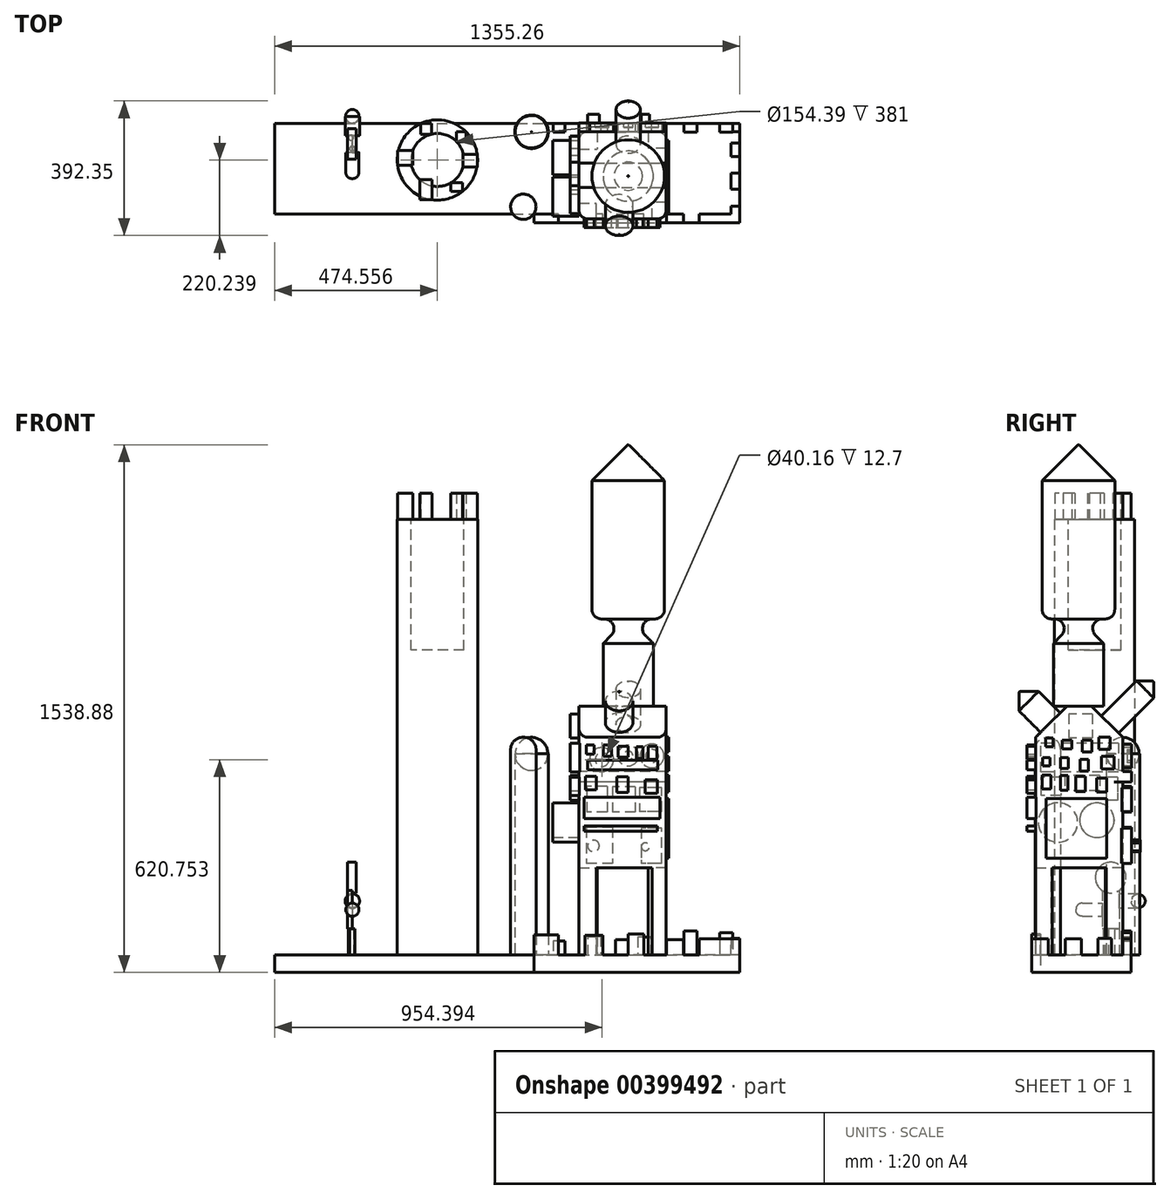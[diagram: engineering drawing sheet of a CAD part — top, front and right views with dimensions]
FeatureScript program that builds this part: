
annotation { "Feature Type Name" : "Feature", "Feature Type Description" : "" }
export const myFeature = defineFeature(function(context is Context, id is Id, definition is map)
    precondition{}
    {
        {
            var Q0;
            Q0=qCreatedBy(makeId("Front.planeOp"),FACE);
            var sketch = newSketch(context, id + "F0", { "sketchPlane" : qUnion([Q0])});
            skLineSegment(sketch, "E0.bottom", {"start": v(-143.4, 414.63) * mm, "end": v(110.6, 414.63) * mm});
            skLineSegment(sketch, "E0.top", {"start": v(-143.4, -93.37) * mm, "end": v(110.6, -93.37) * mm});
            skLineSegment(sketch, "E0.left", {"start": v(-143.4, 414.63) * mm, "end": v(-143.4, -93.37) * mm});
            skLineSegment(sketch, "E0.right", {"start": v(110.6, 414.63) * mm, "end": v(110.6, -93.37) * mm});
            skSolve(sketch);
        }
        {
            var Q0;
            Q0 = qSketchRegion(id + "F0", true);
            extrude(context, id + "F1", {"entities" : qUnion([Q0]), "depth" : 254 * mm});
        }
        {
            var Q0;
            Q0=makeQuery(id+"F1.opExtrude","CAP_EDGE",EDGE,{"disambiguationData":[OSD([sQuery(id+"F0.wireOp",EDGE,"E0.bottom")])],"isStart":false});
            chamfer(context, id + "F2", {"entities" : qUnion([Q0]), "width" : 127 * mm, "tangentPropagation" : true});
        }
        {
            var Q0;
            Q0=makeQuery(id+"F1.opExtrude","CAP_EDGE",EDGE,{"disambiguationData":[OSD([sQuery(id+"F0.wireOp",EDGE,"E0.bottom")])],"isStart":true});
            chamfer(context, id + "F3", {"entities" : qUnion([Q0]), "width" : 127 * mm, "tangentPropagation" : true});
        }
        {
            var Q0;
            {var subQ0=sQuery(id+"F0.wireOp",EDGE,"E0.bottom");Q0=makeQuery(id+"F3.opChamfer","BLEND_EDGE",EDGE,{"blendedFrom":[makeQuery(id+"F1.opExtrude","CAP_EDGE",EDGE,{"disambiguationData":[OSD([subQ0])],"isStart":true}),makeQuery(id+"F2.opChamfer","BLEND_FACE",FACE,{"disambiguationData":[OSD([subQ0])]})],"blendedInto":[makeQuery(id+"F2.opChamfer","BLEND_FACE",FACE,{"disambiguationData":[OSD([subQ0])]})]});}
            chamfer(context, id + "F4", {"entities" : qUnion([Q0]), "width" : 50.8 * mm, "tangentPropagation" : true});
        }
        {
            var Q0;
            Q0=makeQuery(id+"F4.opChamfer","BLEND_FACE",FACE,{"disambiguationData":[OSD([sQuery(id+"F0.wireOp",EDGE,"E0.bottom")])]});
            var sketch = newSketch(context, id + "F5", { "sketchPlane" : qUnion([Q0])});
            skCircle(sketch, "E1", {"center": v(0, -129.26) * mm, "radius": 73.19 * mm});
            skSolve(sketch);
        }
        {
            var Q0;
            Q0 = qSketchRegion(id + "F5", true);
            extrude(context, id + "F6", {"entities" : qUnion([Q0]), "operationType" : NewBodyOperationType.ADD, "depth" : 254 * mm});
        }
        {
            var Q0;
            Q0=makeQuery(id+"F6.opExtrude","CAP_EDGE",EDGE,{"disambiguationData":[OSD([sQuery(id+"F5.wireOp",EDGE,"E1")])],"isStart":false});
            chamfer(context, id + "F7", {"entities" : qUnion([Q0]), "width" : 71.12 * mm, "tangentPropagation" : true});
        }
        {
            var Q0;
            Q0=makeQuery(id+"F1.opExtrude","SWEPT_FACE",FACE,{"disambiguationData":[OSD([sQuery(id+"F0.wireOp",EDGE,"E0.right")])]});
            var sketch = newSketch(context, id + "F8", { "sketchPlane" : qUnion([Q0])});
            skLineSegment(sketch, "E2.bottom", {"start": v(-225.22, 286.05) * mm, "end": v(-203.04, 286.05) * mm});
            skLineSegment(sketch, "E2.top", {"start": v(-225.22, 259.97) * mm, "end": v(-203.04, 259.97) * mm});
            skLineSegment(sketch, "E2.left", {"start": v(-225.22, 286.05) * mm, "end": v(-225.22, 259.97) * mm});
            skLineSegment(sketch, "E2.right", {"start": v(-203.04, 286.05) * mm, "end": v(-203.04, 259.97) * mm});
            skLineSegment(sketch, "E3.bottom", {"start": v(-176.84, 279.59) * mm, "end": v(-149.3, 279.59) * mm});
            skLineSegment(sketch, "E3.top", {"start": v(-176.84, 254.16) * mm, "end": v(-149.3, 254.16) * mm});
            skLineSegment(sketch, "E3.left", {"start": v(-176.84, 279.59) * mm, "end": v(-176.84, 254.16) * mm});
            skLineSegment(sketch, "E3.right", {"start": v(-149.3, 279.59) * mm, "end": v(-149.3, 254.16) * mm});
            skLineSegment(sketch, "E4.bottom", {"start": v(-118.38, 279.83) * mm, "end": v(-89.7, 279.83) * mm});
            skLineSegment(sketch, "E4.top", {"start": v(-118.38, 244.95) * mm, "end": v(-89.7, 244.95) * mm});
            skLineSegment(sketch, "E4.left", {"start": v(-118.38, 279.83) * mm, "end": v(-118.38, 244.95) * mm});
            skLineSegment(sketch, "E4.right", {"start": v(-89.7, 279.83) * mm, "end": v(-89.7, 244.95) * mm});
            skLineSegment(sketch, "E5.bottom", {"start": v(-70.45, 288.39) * mm, "end": v(-36.24, 288.39) * mm});
            skLineSegment(sketch, "E5.top", {"start": v(-70.45, 252.8) * mm, "end": v(-36.24, 252.8) * mm});
            skLineSegment(sketch, "E5.left", {"start": v(-70.45, 288.39) * mm, "end": v(-70.45, 252.8) * mm});
            skLineSegment(sketch, "E5.right", {"start": v(-36.24, 288.39) * mm, "end": v(-36.24, 252.8) * mm});
            skLineSegment(sketch, "E6.bottom", {"start": v(-233.3, 228.9) * mm, "end": v(-212.62, 228.9) * mm});
            skLineSegment(sketch, "E6.top", {"start": v(-233.3, 204) * mm, "end": v(-212.62, 204) * mm});
            skLineSegment(sketch, "E6.left", {"start": v(-233.3, 228.9) * mm, "end": v(-233.3, 204) * mm});
            skLineSegment(sketch, "E6.right", {"start": v(-212.62, 228.9) * mm, "end": v(-212.62, 204) * mm});
            skLineSegment(sketch, "E7.bottom", {"start": v(-181.54, 228.33) * mm, "end": v(-158.71, 228.33) * mm});
            skLineSegment(sketch, "E7.top", {"start": v(-181.54, 196.85) * mm, "end": v(-158.71, 196.85) * mm});
            skLineSegment(sketch, "E7.left", {"start": v(-181.54, 228.33) * mm, "end": v(-181.54, 196.85) * mm});
            skLineSegment(sketch, "E7.right", {"start": v(-158.71, 228.33) * mm, "end": v(-158.71, 196.85) * mm});
            skLineSegment(sketch, "E8.bottom", {"start": v(-125.12, 222.84) * mm, "end": v(-100.62, 222.84) * mm});
            skLineSegment(sketch, "E8.top", {"start": v(-125.12, 188.82) * mm, "end": v(-100.62, 188.82) * mm});
            skLineSegment(sketch, "E8.left", {"start": v(-125.12, 222.84) * mm, "end": v(-125.12, 188.82) * mm});
            skLineSegment(sketch, "E8.right", {"start": v(-100.62, 222.84) * mm, "end": v(-100.62, 188.82) * mm});
            skLineSegment(sketch, "E9.bottom", {"start": v(-62.28, 231.84) * mm, "end": v(-25.23, 231.84) * mm});
            skLineSegment(sketch, "E9.top", {"start": v(-62.28, 195.23) * mm, "end": v(-25.23, 195.23) * mm});
            skLineSegment(sketch, "E9.left", {"start": v(-62.28, 231.84) * mm, "end": v(-62.28, 195.23) * mm});
            skLineSegment(sketch, "E9.right", {"start": v(-25.23, 231.84) * mm, "end": v(-25.23, 195.23) * mm});
            skLineSegment(sketch, "E10.bottom", {"start": v(-235.32, 177.96) * mm, "end": v(-210, 177.96) * mm});
            skLineSegment(sketch, "E10.top", {"start": v(-235.32, 137.2) * mm, "end": v(-210, 137.2) * mm});
            skLineSegment(sketch, "E10.left", {"start": v(-235.32, 177.96) * mm, "end": v(-235.32, 137.2) * mm});
            skLineSegment(sketch, "E10.right", {"start": v(-210, 177.96) * mm, "end": v(-210, 137.2) * mm});
            skLineSegment(sketch, "E11.bottom", {"start": v(-181.54, 175.72) * mm, "end": v(-160.61, 175.72) * mm});
            skLineSegment(sketch, "E11.top", {"start": v(-181.54, 133.6) * mm, "end": v(-160.61, 133.6) * mm});
            skLineSegment(sketch, "E11.left", {"start": v(-181.54, 175.72) * mm, "end": v(-181.54, 133.6) * mm});
            skLineSegment(sketch, "E11.right", {"start": v(-160.61, 175.72) * mm, "end": v(-160.61, 133.6) * mm});
            skLineSegment(sketch, "E12.bottom", {"start": v(-136.85, 173.47) * mm, "end": v(-109.71, 173.47) * mm});
            skLineSegment(sketch, "E12.top", {"start": v(-136.85, 128.81) * mm, "end": v(-109.71, 128.81) * mm});
            skLineSegment(sketch, "E12.left", {"start": v(-136.85, 173.47) * mm, "end": v(-136.85, 128.81) * mm});
            skLineSegment(sketch, "E12.right", {"start": v(-109.71, 173.47) * mm, "end": v(-109.71, 128.81) * mm});
            skLineSegment(sketch, "E13.bottom", {"start": v(-76.4, 168.47) * mm, "end": v(-47.08, 168.47) * mm});
            skLineSegment(sketch, "E13.top", {"start": v(-76.4, 128.2) * mm, "end": v(-47.08, 128.2) * mm});
            skLineSegment(sketch, "E13.left", {"start": v(-76.4, 168.47) * mm, "end": v(-76.4, 128.2) * mm});
            skLineSegment(sketch, "E13.right", {"start": v(-47.08, 168.47) * mm, "end": v(-47.08, 128.2) * mm});
            skLineSegment(sketch, "E14.bottom", {"start": v(-223, 109.59) * mm, "end": v(-46.93, 109.59) * mm});
            skLineSegment(sketch, "E14.top", {"start": v(-223, -64.96) * mm, "end": v(-46.93, -64.96) * mm});
            skLineSegment(sketch, "E14.left", {"start": v(-223, 109.59) * mm, "end": v(-223, -64.96) * mm});
            skLineSegment(sketch, "E14.right", {"start": v(-46.93, 109.59) * mm, "end": v(-46.93, -64.96) * mm});
            skSolve(sketch);
        }
        {
            var Q0;
            Q0 = qSketchRegion(id + "F8", true);
            extrude(context, id + "F9", {"entities" : qUnion([Q0]), "operationType" : NewBodyOperationType.ADD, "depth" : 7.62 * mm});
        }
        {
            var Q0;
            Q0=makeQuery(id+"F3.opChamfer","BLEND_FACE",FACE,{"disambiguationData":[OSD([sQuery(id+"F0.wireOp",EDGE,"E0.bottom")])]});
            var sketch = newSketch(context, id + "F10", { "sketchPlane" : qUnion([Q0])});
            skCircle(sketch, "E15", {"center": v(0, 256.46) * mm, "radius": 35.35 * mm});
            skSolve(sketch);
        }
        {
            var Q0;
            Q0 = qSketchRegion(id + "F10", true);
            extrude(context, id + "F11", {"entities" : qUnion([Q0]), "operationType" : NewBodyOperationType.ADD, "depth" : 177.8 * mm});
        }
        {
            var Q0;
            Q0=makeQuery(id+"F11.opExtrude","CAP_EDGE",EDGE,{"disambiguationData":[OSD([sQuery(id+"F10.wireOp",EDGE,"E15")])],"isStart":false});
            chamfer(context, id + "F12", {"entities" : qUnion([Q0]), "width" : 33.02 * mm, "tangentPropagation" : true});
        }
        {
            var Q0;
            Q0=makeQuery(id+"F2.opChamfer","BLEND_FACE",FACE,{"disambiguationData":[OSD([sQuery(id+"F0.wireOp",EDGE,"E0.bottom")])]});
            var sketch = newSketch(context, id + "F13", { "sketchPlane" : qUnion([Q0])});
            skCircle(sketch, "E16", {"center": v(-26.41, 84.26) * mm, "radius": 40.19 * mm});
            skSolve(sketch);
        }
        {
            var Q0;
            Q0 = qSketchRegion(id + "F13", true);
            extrude(context, id + "F14", {"entities" : qUnion([Q0]), "operationType" : NewBodyOperationType.ADD, "depth" : 127 * mm});
        }
        {
            var Q0;
            Q0=makeQuery(id+"F14.opExtrude","CAP_FACE",FACE,{"disambiguationData":[OSD([sQuery(id+"F13.wireOp",EDGE,"E16")])],"isStart":false});
            chamfer(context, id + "F15", {"entities" : qUnion([Q0]), "width" : 38.1 * mm, "tangentPropagation" : true});
        }
        {
            var Q0;
            Q0=makeQuery(id+"F1.opExtrude","CAP_FACE",FACE,{"disambiguationData":[OSD([sQuery(id+"F0.wireOp",EDGE,"E0.bottom"),sQuery(id+"F0.wireOp",EDGE,"E0.top"),sQuery(id+"F0.wireOp",EDGE,"E0.left"),sQuery(id+"F0.wireOp",EDGE,"E0.right")])],"isStart":false});
            var sketch = newSketch(context, id + "F16", { "sketchPlane" : qUnion([Q0])});
            skLineSegment(sketch, "E17.bottom", {"start": v(-122.31, 265.6) * mm, "end": v(-99.77, 265.6) * mm});
            skLineSegment(sketch, "E17.top", {"start": v(-122.31, 238.2) * mm, "end": v(-99.77, 238.2) * mm});
            skLineSegment(sketch, "E17.left", {"start": v(-122.31, 265.6) * mm, "end": v(-122.31, 238.2) * mm});
            skLineSegment(sketch, "E17.right", {"start": v(-99.77, 265.6) * mm, "end": v(-99.77, 238.2) * mm});
            skLineSegment(sketch, "E18.bottom", {"start": v(-72.06, 264.99) * mm, "end": v(-48.83, 264.99) * mm});
            skLineSegment(sketch, "E18.top", {"start": v(-72.06, 232.03) * mm, "end": v(-48.83, 232.03) * mm});
            skLineSegment(sketch, "E18.left", {"start": v(-72.06, 264.99) * mm, "end": v(-72.06, 232.03) * mm});
            skLineSegment(sketch, "E18.right", {"start": v(-48.83, 264.99) * mm, "end": v(-48.83, 232.03) * mm});
            skLineSegment(sketch, "E19.bottom", {"start": v(-29, 261.13) * mm, "end": v(0, 261.13) * mm});
            skLineSegment(sketch, "E19.top", {"start": v(-29, 229.2) * mm, "end": v(0, 229.2) * mm});
            skLineSegment(sketch, "E19.left", {"start": v(-29, 261.13) * mm, "end": v(-29, 229.2) * mm});
            skLineSegment(sketch, "E19.right", {"start": v(0, 261.13) * mm, "end": v(0, 229.2) * mm});
            skLineSegment(sketch, "E20.bottom", {"start": v(23.92, 260.2) * mm, "end": v(42.97, 260.2) * mm});
            skLineSegment(sketch, "E20.top", {"start": v(23.92, 226.37) * mm, "end": v(42.97, 226.37) * mm});
            skLineSegment(sketch, "E20.left", {"start": v(23.92, 260.2) * mm, "end": v(23.92, 226.37) * mm});
            skLineSegment(sketch, "E20.right", {"start": v(42.97, 260.2) * mm, "end": v(42.97, 226.37) * mm});
            skLineSegment(sketch, "E21.bottom", {"start": v(58.09, 261.53) * mm, "end": v(83.35, 261.53) * mm});
            skLineSegment(sketch, "E21.top", {"start": v(58.09, 222.84) * mm, "end": v(83.35, 222.84) * mm});
            skLineSegment(sketch, "E21.left", {"start": v(58.09, 261.53) * mm, "end": v(58.09, 222.84) * mm});
            skLineSegment(sketch, "E21.right", {"start": v(83.35, 261.53) * mm, "end": v(83.35, 222.84) * mm});
            skLineSegment(sketch, "E22.bottom", {"start": v(-125.17, 174.16) * mm, "end": v(-93.2, 174.16) * mm});
            skLineSegment(sketch, "E22.top", {"start": v(-125.17, 134.66) * mm, "end": v(-93.2, 134.66) * mm});
            skLineSegment(sketch, "E22.left", {"start": v(-125.17, 174.16) * mm, "end": v(-125.17, 134.66) * mm});
            skLineSegment(sketch, "E22.right", {"start": v(-93.2, 174.16) * mm, "end": v(-93.2, 134.66) * mm});
            skLineSegment(sketch, "E23.bottom", {"start": v(49.06, 163.98) * mm, "end": v(85.04, 163.98) * mm});
            skLineSegment(sketch, "E23.top", {"start": v(49.06, 124) * mm, "end": v(85.04, 124) * mm});
            skLineSegment(sketch, "E23.left", {"start": v(49.06, 163.98) * mm, "end": v(49.06, 124) * mm});
            skLineSegment(sketch, "E23.right", {"start": v(85.04, 163.98) * mm, "end": v(85.04, 124) * mm});
            skLineSegment(sketch, "E24.bottom", {"start": v(-32.88, 172.55) * mm, "end": v(0, 172.55) * mm});
            skLineSegment(sketch, "E24.top", {"start": v(-32.88, 126.95) * mm, "end": v(0, 126.95) * mm});
            skLineSegment(sketch, "E24.left", {"start": v(-32.88, 172.55) * mm, "end": v(-32.88, 126.95) * mm});
            skLineSegment(sketch, "E24.right", {"start": v(0, 172.55) * mm, "end": v(0, 126.95) * mm});
            skLineSegment(sketch, "E25.bottom", {"start": v(-128.46, 112.9) * mm, "end": v(92.51, 112.9) * mm});
            skLineSegment(sketch, "E25.top", {"start": v(-128.46, 50.48) * mm, "end": v(92.51, 50.48) * mm});
            skLineSegment(sketch, "E25.left", {"start": v(-128.46, 112.9) * mm, "end": v(-128.46, 50.48) * mm});
            skLineSegment(sketch, "E25.right", {"start": v(92.51, 112.9) * mm, "end": v(92.51, 50.48) * mm});
            skSolve(sketch);
        }
        {
            var Q0;
            Q0 = qSketchRegion(id + "F16", true);
            extrude(context, id + "F17", {"entities" : qUnion([Q0]), "operationType" : NewBodyOperationType.ADD, "depth" : 25.4 * mm});
        }
        {
            var Q0;
            Q0=makeQuery(id+"F1.opExtrude","CAP_FACE",FACE,{"disambiguationData":[OSD([sQuery(id+"F0.wireOp",EDGE,"E0.bottom"),sQuery(id+"F0.wireOp",EDGE,"E0.top"),sQuery(id+"F0.wireOp",EDGE,"E0.left"),sQuery(id+"F0.wireOp",EDGE,"E0.right")])],"isStart":false});
            var sketch = newSketch(context, id + "F18", { "sketchPlane" : qUnion([Q0])});
            skLineSegment(sketch, "E26.bottom", {"start": v(-118.13, 221.26) * mm, "end": v(86.47, 221.26) * mm});
            skLineSegment(sketch, "E26.top", {"start": v(-118.13, 192.32) * mm, "end": v(86.47, 192.32) * mm});
            skLineSegment(sketch, "E26.left", {"start": v(-118.13, 221.26) * mm, "end": v(-118.13, 192.32) * mm});
            skLineSegment(sketch, "E26.right", {"start": v(86.47, 221.26) * mm, "end": v(86.47, 192.32) * mm});
            skLineSegment(sketch, "E27.bottom", {"start": v(-128.46, 29.24) * mm, "end": v(85.04, 29.24) * mm});
            skLineSegment(sketch, "E27.top", {"start": v(-128.46, 13.54) * mm, "end": v(85.04, 13.54) * mm});
            skLineSegment(sketch, "E27.left", {"start": v(-128.46, 29.24) * mm, "end": v(-128.46, 13.54) * mm});
            skLineSegment(sketch, "E27.right", {"start": v(85.04, 29.24) * mm, "end": v(85.04, 13.54) * mm});
            skSolve(sketch);
        }
        {
            var Q0;
            Q0 = qSketchRegion(id + "F18", true);
            extrude(context, id + "F19", {"entities" : qUnion([Q0]), "operationType" : NewBodyOperationType.ADD, "depth" : 25.4 * mm});
        }
        {
            var Q0;
            Q0=makeQuery(id+"F1.opExtrude","CAP_FACE",FACE,{"disambiguationData":[OSD([sQuery(id+"F0.wireOp",EDGE,"E0.bottom"),sQuery(id+"F0.wireOp",EDGE,"E0.top"),sQuery(id+"F0.wireOp",EDGE,"E0.left"),sQuery(id+"F0.wireOp",EDGE,"E0.right")])],"isStart":true});
            var sketch = newSketch(context, id + "F20", { "sketchPlane" : qUnion([Q0])});
            skLineSegment(sketch, "E28.bottom", {"start": v(-110.6, 187.39) * mm, "end": v(143.4, 187.39) * mm});
            skLineSegment(sketch, "E28.top", {"start": v(-110.6, 157.9) * mm, "end": v(143.4, 157.9) * mm});
            skLineSegment(sketch, "E28.left", {"start": v(-110.6, 187.39) * mm, "end": v(-110.6, 157.9) * mm});
            skLineSegment(sketch, "E28.right", {"start": v(143.4, 187.39) * mm, "end": v(143.4, 157.9) * mm});
            skCircle(sketch, "E29", {"center": v(-69.46, 233.42) * mm, "radius": 34.62 * mm});
            skCircle(sketch, "E30", {"center": v(0, 234.1) * mm, "radius": 30.15 * mm});
            skCircle(sketch, "E31", {"center": v(77.39, 222.47) * mm, "radius": 35 * mm});
            skSolve(sketch);
        }
        {
            var Q0;
            Q0 = qSketchRegion(id + "F20", true);
            extrude(context, id + "F21", {"entities" : qUnion([Q0]), "operationType" : NewBodyOperationType.ADD, "depth" : 25.4 * mm});
        }
        {
            var Q0;
            Q0=makeQuery(id+"F21.opExtrude","CAP_FACE",FACE,{"disambiguationData":[OSD([sQuery(id+"F20.wireOp",EDGE,"E29")])],"isStart":false});
            var sketch = newSketch(context, id + "F22", { "sketchPlane" : qUnion([Q0])});
            skCircle(sketch, "E32", {"center": v(-69.46, 233.42) * mm, "radius": 18.8 * mm});
            skCircle(sketch, "E33", {"center": v(0, 234.27) * mm, "radius": 13.26 * mm});
            skCircle(sketch, "E34", {"center": v(76.02, 222.58) * mm, "radius": 20.08 * mm});
            skSolve(sketch);
        }
        {
            var Q0;
            Q0 = qSketchRegion(id + "F22", true);
            extrude(context, id + "F23", {"entities" : qUnion([Q0]), "operationType" : NewBodyOperationType.REMOVE, "oppositeDirection" : true, "depth" : 12.7 * mm});
        }
        {
            var Q0;
            {var subQ0=sQuery(id+"F0.wireOp",EDGE,"E0.top");var subQ1=sQuery(id+"F0.wireOp",EDGE,"E0.right");var subQ2=sQuery(id+"F0.wireOp",EDGE,"E0.left");Q0=makeQuery(id+"F21.boolean.opBoolean","SPLIT",FACE,{"disambiguationData":[TD([makeQuery(id+"F1.opExtrude","SWEPT_FACE",FACE,{"disambiguationData":[OSD([subQ0])]})])],"derivedFrom":makeQuery(id+"F1.opExtrude","CAP_FACE",FACE,{"disambiguationData":[OSD([sQuery(id+"F0.wireOp",EDGE,"E0.bottom"),subQ0,subQ2,subQ1])],"isStart":true})});}
            var sketch = newSketch(context, id + "F24", { "sketchPlane" : qUnion([Q0])});
            skLineSegment(sketch, "E35.bottom", {"start": v(-97.46, 140.8) * mm, "end": v(-33.08, 140.8) * mm});
            skLineSegment(sketch, "E35.top", {"start": v(-97.46, 70.86) * mm, "end": v(-33.08, 70.86) * mm});
            skLineSegment(sketch, "E35.left", {"start": v(-97.46, 140.8) * mm, "end": v(-97.46, 70.86) * mm});
            skLineSegment(sketch, "E35.right", {"start": v(-33.08, 140.8) * mm, "end": v(-33.08, 70.86) * mm});
            skLineSegment(sketch, "E36.bottom", {"start": v(-20.64, 143.08) * mm, "end": v(45.29, 143.08) * mm});
            skLineSegment(sketch, "E36.top", {"start": v(-20.64, 69.47) * mm, "end": v(45.29, 69.47) * mm});
            skLineSegment(sketch, "E36.left", {"start": v(-20.64, 143.08) * mm, "end": v(-20.64, 69.47) * mm});
            skLineSegment(sketch, "E36.right", {"start": v(45.29, 143.08) * mm, "end": v(45.29, 69.47) * mm});
            skLineSegment(sketch, "E37.bottom", {"start": v(61.47, 145.12) * mm, "end": v(121.04, 145.12) * mm});
            skLineSegment(sketch, "E37.top", {"start": v(61.47, 69.47) * mm, "end": v(121.04, 69.47) * mm});
            skLineSegment(sketch, "E37.left", {"start": v(61.47, 145.12) * mm, "end": v(61.47, 69.47) * mm});
            skLineSegment(sketch, "E37.right", {"start": v(121.04, 145.12) * mm, "end": v(121.04, 69.47) * mm});
            skLineSegment(sketch, "E38.bottom", {"start": v(-98.23, 22.27) * mm, "end": v(-38.45, 22.27) * mm});
            skLineSegment(sketch, "E38.top", {"start": v(-98.23, -79.94) * mm, "end": v(-38.45, -79.94) * mm});
            skLineSegment(sketch, "E38.left", {"start": v(-98.23, 22.27) * mm, "end": v(-98.23, -79.94) * mm});
            skLineSegment(sketch, "E38.right", {"start": v(-38.45, 22.27) * mm, "end": v(-38.45, -79.94) * mm});
            skLineSegment(sketch, "E39.bottom", {"start": v(45.29, 25.2) * mm, "end": v(121.59, 25.2) * mm});
            skLineSegment(sketch, "E39.top", {"start": v(45.29, -79.94) * mm, "end": v(121.59, -79.94) * mm});
            skLineSegment(sketch, "E39.left", {"start": v(45.29, 25.2) * mm, "end": v(45.29, -79.94) * mm});
            skLineSegment(sketch, "E39.right", {"start": v(121.59, 25.2) * mm, "end": v(121.59, -79.94) * mm});
            skSolve(sketch);
        }
        {
            var Q0;
            Q0 = qSketchRegion(id + "F24", true);
            extrude(context, id + "F25", {"entities" : qUnion([Q0]), "operationType" : NewBodyOperationType.ADD, "depth" : 25.4 * mm});
        }
        {
            var Q0;
            Q0=makeQuery(id+"F25.opExtrude","CAP_FACE",FACE,{"disambiguationData":[OSD([sQuery(id+"F24.wireOp",EDGE,"E38.bottom"),sQuery(id+"F24.wireOp",EDGE,"E38.top"),sQuery(id+"F24.wireOp",EDGE,"E38.left"),sQuery(id+"F24.wireOp",EDGE,"E38.right")])],"isStart":false});
            var sketch = newSketch(context, id + "F26", { "sketchPlane" : qUnion([Q0])});
            skCircle(sketch, "E40", {"center": v(-49.85, -31.53) * mm, "radius": 11.57 * mm});
            skCircle(sketch, "E41", {"center": v(101.37, -29.1) * mm, "radius": 16.9 * mm});
            skSolve(sketch);
        }
        {
            var Q0;
            Q0 = qSketchRegion(id + "F26", true);
            extrude(context, id + "F27", {"entities" : qUnion([Q0]), "operationType" : NewBodyOperationType.ADD, "depth" : 25.4 * mm});
        }
        {
            var Q0;
            Q0=makeQuery(id+"F21.boolean.opBoolean","MERGE",FACE,{"derivedFrom":[makeQuery(id+"F1.opExtrude","SWEPT_FACE",FACE,{"disambiguationData":[OSD([sQuery(id+"F0.wireOp",EDGE,"E0.left")])]}),makeQuery(id+"F21.opExtrude","SWEPT_FACE",FACE,{"disambiguationData":[OSD([sQuery(id+"F20.wireOp",EDGE,"E28.right")])]})]});
            var sketch = newSketch(context, id + "F28", { "sketchPlane" : qUnion([Q0])});
            skLineSegment(sketch, "E42.bottom", {"start": v(88.44, 356.02) * mm, "end": v(156.94, 356.02) * mm});
            skLineSegment(sketch, "E42.top", {"start": v(88.44, 285.69) * mm, "end": v(156.94, 285.69) * mm});
            skLineSegment(sketch, "E42.left", {"start": v(88.44, 356.02) * mm, "end": v(88.44, 285.69) * mm});
            skLineSegment(sketch, "E42.right", {"start": v(156.94, 356.02) * mm, "end": v(156.94, 285.69) * mm});
            skLineSegment(sketch, "E43.bottom", {"start": v(13.07, 270.94) * mm, "end": v(238.51, 270.94) * mm});
            skLineSegment(sketch, "E43.top", {"start": v(13.07, 186.34) * mm, "end": v(238.51, 186.34) * mm});
            skLineSegment(sketch, "E43.left", {"start": v(13.07, 270.94) * mm, "end": v(13.07, 186.34) * mm});
            skLineSegment(sketch, "E43.right", {"start": v(238.51, 270.94) * mm, "end": v(238.51, 186.34) * mm});
            skLineSegment(sketch, "E44.bottom", {"start": v(15.33, 171.67) * mm, "end": v(48.67, 171.67) * mm});
            skLineSegment(sketch, "E44.top", {"start": v(15.33, 104.41) * mm, "end": v(48.67, 104.41) * mm});
            skLineSegment(sketch, "E44.left", {"start": v(15.33, 171.67) * mm, "end": v(15.33, 104.41) * mm});
            skLineSegment(sketch, "E44.right", {"start": v(48.67, 171.67) * mm, "end": v(48.67, 104.41) * mm});
            skLineSegment(sketch, "E45.bottom", {"start": v(180.97, 170.66) * mm, "end": v(237.3, 170.66) * mm});
            skLineSegment(sketch, "E45.top", {"start": v(180.97, 117.3) * mm, "end": v(237.3, 117.3) * mm});
            skLineSegment(sketch, "E45.left", {"start": v(180.97, 170.66) * mm, "end": v(180.97, 117.3) * mm});
            skLineSegment(sketch, "E45.right", {"start": v(237.3, 170.66) * mm, "end": v(237.3, 117.3) * mm});
            skLineSegment(sketch, "E46.bottom", {"start": v(67.95, 176.02) * mm, "end": v(169.16, 176.02) * mm});
            skLineSegment(sketch, "E46.top", {"start": v(67.95, 131.54) * mm, "end": v(169.16, 131.54) * mm});
            skLineSegment(sketch, "E46.left", {"start": v(67.95, 176.02) * mm, "end": v(67.95, 131.54) * mm});
            skLineSegment(sketch, "E46.right", {"start": v(169.16, 176.02) * mm, "end": v(169.16, 131.54) * mm});
            skSolve(sketch);
        }
        {
            var Q0;
            Q0 = qSketchRegion(id + "F28", true);
            extrude(context, id + "F29", {"entities" : qUnion([Q0]), "operationType" : NewBodyOperationType.ADD, "depth" : 25.4 * mm});
        }
        {
            var Q0;
            Q0=makeQuery(id+"F6.opExtrude","CAP_FACE",FACE,{"disambiguationData":[OSD([sQuery(id+"F5.wireOp",EDGE,"E1")])],"isStart":false});
            var sketch = newSketch(context, id + "F30", { "sketchPlane" : qUnion([Q0])});
            skCircle(sketch, "E47", {"center": v(0, -129.26) * mm, "radius": 105.7 * mm});
            skSolve(sketch);
        }
        {
            var Q0;
            Q0 = qSketchRegion(id + "F30", true);
            extrude(context, id + "F31", {"entities" : qUnion([Q0]), "operationType" : NewBodyOperationType.ADD, "depth" : 508 * mm});
        }
        {
            var Q0;
            Q0=makeQuery(id+"F31.opExtrude","CAP_FACE",FACE,{"disambiguationData":[OSD([sQuery(id+"F30.wireOp",EDGE,"E47")])],"isStart":false});
            chamfer(context, id + "F32", {"entities" : qUnion([Q0]), "width" : 104.14 * mm, "tangentPropagation" : true});
        }
        {
            var Q0;
            Q0=makeQuery(id+"F31.opExtrude","CAP_FACE",FACE,{"disambiguationData":[OSD([sQuery(id+"F30.wireOp",EDGE,"E47")])],"isStart":true});
            fillet(context, id + "F33", {"entities" : qUnion([Q0]), "radius" : 27.94 * mm, "tangentPropagation" : true, "allowEdgeOverflow" : false});
        }
        {
            var Q0;
            Q0=makeQuery(id+"F1.opExtrude","SWEPT_FACE",FACE,{"disambiguationData":[OSD([sQuery(id+"F0.wireOp",EDGE,"E0.top")])]});
            var sketch = newSketch(context, id + "F34", { "sketchPlane" : qUnion([Q0])});
            skLineSegment(sketch, "E48.bottom", {"start": v(-143.4, 0) * mm, "end": v(-90.9, 0) * mm});
            skLineSegment(sketch, "E48.top", {"start": v(-143.4, 50.29) * mm, "end": v(-90.9, 50.29) * mm});
            skLineSegment(sketch, "E48.left", {"start": v(-143.4, 0) * mm, "end": v(-143.4, 50.29) * mm});
            skLineSegment(sketch, "E48.right", {"start": v(-90.9, 0) * mm, "end": v(-90.9, 50.29) * mm});
            skLineSegment(sketch, "E49.bottom", {"start": v(110.6, 0) * mm, "end": v(57.9, 0) * mm});
            skLineSegment(sketch, "E49.top", {"start": v(110.6, 48.35) * mm, "end": v(57.9, 48.35) * mm});
            skLineSegment(sketch, "E49.left", {"start": v(110.6, 0) * mm, "end": v(110.6, 48.35) * mm});
            skLineSegment(sketch, "E49.right", {"start": v(57.9, 0) * mm, "end": v(57.9, 48.35) * mm});
            skLineSegment(sketch, "E50.bottom", {"start": v(-143.4, 254) * mm, "end": v(-92.3, 254) * mm});
            skLineSegment(sketch, "E50.top", {"start": v(-143.4, 208.6) * mm, "end": v(-92.3, 208.6) * mm});
            skLineSegment(sketch, "E50.left", {"start": v(-143.4, 254) * mm, "end": v(-143.4, 208.6) * mm});
            skLineSegment(sketch, "E50.right", {"start": v(-92.3, 254) * mm, "end": v(-92.3, 208.6) * mm});
            skLineSegment(sketch, "E51.bottom", {"start": v(110.6, 254) * mm, "end": v(69.29, 254) * mm});
            skLineSegment(sketch, "E51.top", {"start": v(110.6, 205.76) * mm, "end": v(69.29, 205.76) * mm});
            skLineSegment(sketch, "E51.left", {"start": v(110.6, 254) * mm, "end": v(110.6, 205.76) * mm});
            skLineSegment(sketch, "E51.right", {"start": v(69.29, 254) * mm, "end": v(69.29, 205.76) * mm});
            skSolve(sketch);
        }
        {
            var Q0;
            Q0 = qSketchRegion(id + "F34", true);
            extrude(context, id + "F35", {"entities" : qUnion([Q0]), "operationType" : NewBodyOperationType.ADD, "depth" : 254 * mm});
        }
        {
            var Q0;
            {var subQ0=sQuery(id+"F0.wireOp",EDGE,"E0.left");var subQ1=sQuery(id+"F0.wireOp",EDGE,"E0.top");Q0=makeQuery(id+"F35.boolean.opBoolean","MERGE",EDGE,{"derivedFrom":[makeQuery(id+"F21.boolean.opBoolean","SPLIT",EDGE,{"disambiguationData":[TD([makeQuery(id+"F1.opExtrude","SWEPT_FACE",FACE,{"disambiguationData":[OSD([subQ1])]})])],"derivedFrom":makeQuery(id+"F1.opExtrude","CAP_EDGE",EDGE,{"disambiguationData":[OSD([subQ0])],"isStart":true})}),makeQuery(id+"F35.opExtrude","SWEPT_EDGE",EDGE,{"disambiguationData":[OSD([sQuery(id+"F34.wireOp",EDGE,"E48.bottom"),sQuery(id+"F34.wireOp",EDGE,"E48.left")])]})]});}
            fillet(context, id + "F36", {"entities" : qUnion([Q0]), "radius" : 25.4 * mm, "tangentPropagation" : true, "allowEdgeOverflow" : false});
        }
        {
            var Q0;
            Q0=makeQuery(id+"F35.boolean.opBoolean","MERGE",EDGE,{"derivedFrom":[makeQuery(id+"F1.opExtrude","CAP_EDGE",EDGE,{"disambiguationData":[OSD([sQuery(id+"F0.wireOp",EDGE,"E0.left")])],"isStart":false}),makeQuery(id+"F35.opExtrude","SWEPT_EDGE",EDGE,{"disambiguationData":[OSD([sQuery(id+"F34.wireOp",EDGE,"E50.bottom"),sQuery(id+"F34.wireOp",EDGE,"E50.left")])]})]});
            fillet(context, id + "F37", {"entities" : qUnion([Q0]), "radius" : 25.4 * mm, "tangentPropagation" : true, "allowEdgeOverflow" : false});
        }
        {
            var Q0;
            Q0=makeQuery(id+"F35.boolean.opBoolean","MERGE",EDGE,{"derivedFrom":[makeQuery(id+"F1.opExtrude","CAP_EDGE",EDGE,{"disambiguationData":[OSD([sQuery(id+"F0.wireOp",EDGE,"E0.right")])],"isStart":false}),makeQuery(id+"F35.opExtrude","SWEPT_EDGE",EDGE,{"disambiguationData":[OSD([sQuery(id+"F34.wireOp",EDGE,"E51.bottom"),sQuery(id+"F34.wireOp",EDGE,"E51.left")])]})]});
            fillet(context, id + "F38", {"entities" : qUnion([Q0]), "radius" : 25.4 * mm, "tangentPropagation" : true, "allowEdgeOverflow" : false});
        }
        {
            var Q0;
            {var subQ0=sQuery(id+"F0.wireOp",EDGE,"E0.right");var subQ1=sQuery(id+"F0.wireOp",EDGE,"E0.top");Q0=makeQuery(id+"F35.boolean.opBoolean","MERGE",EDGE,{"derivedFrom":[makeQuery(id+"F21.boolean.opBoolean","SPLIT",EDGE,{"disambiguationData":[TD([makeQuery(id+"F1.opExtrude","SWEPT_FACE",FACE,{"disambiguationData":[OSD([subQ1])]})])],"derivedFrom":makeQuery(id+"F1.opExtrude","CAP_EDGE",EDGE,{"disambiguationData":[OSD([subQ0])],"isStart":true})}),makeQuery(id+"F35.opExtrude","SWEPT_EDGE",EDGE,{"disambiguationData":[OSD([sQuery(id+"F34.wireOp",EDGE,"E49.bottom"),sQuery(id+"F34.wireOp",EDGE,"E49.left")])]})]});}
            fillet(context, id + "F39", {"entities" : qUnion([Q0]), "radius" : 25.4 * mm, "tangentPropagation" : true, "allowEdgeOverflow" : false});
        }
        {
            var Q0;
            Q0=makeQuery(id+"F35.boolean.opBoolean","MERGE",FACE,{"derivedFrom":[makeQuery(id+"F21.boolean.opBoolean","MERGE",FACE,{"derivedFrom":[makeQuery(id+"F1.opExtrude","SWEPT_FACE",FACE,{"disambiguationData":[OSD([sQuery(id+"F0.wireOp",EDGE,"E0.left")])]}),makeQuery(id+"F21.opExtrude","SWEPT_FACE",FACE,{"disambiguationData":[OSD([sQuery(id+"F20.wireOp",EDGE,"E28.right")])]})]}),makeQuery(id+"F35.opExtrude","SWEPT_FACE",FACE,{"disambiguationData":[OSD([sQuery(id+"F34.wireOp",EDGE,"E48.left")])]}),makeQuery(id+"F35.opExtrude","SWEPT_FACE",FACE,{"disambiguationData":[OSD([sQuery(id+"F34.wireOp",EDGE,"E50.left")])]})]});
            var sketch = newSketch(context, id + "F40", { "sketchPlane" : qUnion([Q0])});
            skCircle(sketch, "E52", {"center": v(75.58, 45.88) * mm, "radius": 50.24 * mm});
            skCircle(sketch, "E53", {"center": v(189.02, 39.25) * mm, "radius": 57.35 * mm});
            skSolve(sketch);
        }
        {
            var Q0;
            Q0 = qSketchRegion(id + "F40", true);
            extrude(context, id + "F41", {"entities" : qUnion([Q0]), "operationType" : NewBodyOperationType.ADD, "depth" : 76.2 * mm});
        }
        {
            var Q0;
            Q0=makeQuery(id+"F35.opExtrude","CAP_FACE",FACE,{"disambiguationData":[OSD([sQuery(id+"F34.wireOp",EDGE,"E48.bottom"),sQuery(id+"F34.wireOp",EDGE,"E48.top"),sQuery(id+"F34.wireOp",EDGE,"E48.left"),sQuery(id+"F34.wireOp",EDGE,"E48.right")])],"isStart":false});
            var sketch = newSketch(context, id + "F42", { "sketchPlane" : qUnion([Q0])});
            skLineSegment(sketch, "E54.bottom", {"start": v(-268.4, -24.66) * mm, "end": v(324.85, -24.66) * mm});
            skLineSegment(sketch, "E54.top", {"start": v(-268.4, 265.2) * mm, "end": v(324.85, 265.2) * mm});
            skLineSegment(sketch, "E54.left", {"start": v(-268.4, -24.66) * mm, "end": v(-268.4, 265.2) * mm});
            skLineSegment(sketch, "E54.right", {"start": v(324.85, -24.66) * mm, "end": v(324.85, 265.2) * mm});
            skSolve(sketch);
        }
        {
            var Q0;
            Q0 = qSketchRegion(id + "F42", true);
            extrude(context, id + "F43", {"entities" : qUnion([Q0]), "operationType" : NewBodyOperationType.ADD, "depth" : 50.8 * mm});
        }
        {
            var Q0;
            Q0=makeQuery(id+"F43.opExtrude","SWEPT_FACE",FACE,{"disambiguationData":[OSD([sQuery(id+"F42.wireOp",EDGE,"E54.bottom")])]});
            var sketch = newSketch(context, id + "F44", { "sketchPlane" : qUnion([Q0])});
            skLineSegment(sketch, "E55.bottom", {"start": v(-304.3, -282.37) * mm, "end": v(-267.1, -282.37) * mm});
            skLineSegment(sketch, "E55.top", {"start": v(-304.3, -398.17) * mm, "end": v(-267.1, -398.17) * mm});
            skLineSegment(sketch, "E55.left", {"start": v(-304.3, -282.37) * mm, "end": v(-304.3, -398.17) * mm});
            skLineSegment(sketch, "E55.right", {"start": v(-267.1, -282.37) * mm, "end": v(-267.1, -398.17) * mm});
            skLineSegment(sketch, "E56.bottom", {"start": v(-200.97, -277.03) * mm, "end": v(-162.48, -277.03) * mm});
            skLineSegment(sketch, "E56.top", {"start": v(-200.97, -398.17) * mm, "end": v(-162.48, -398.17) * mm});
            skLineSegment(sketch, "E56.left", {"start": v(-200.97, -277.03) * mm, "end": v(-200.97, -398.17) * mm});
            skLineSegment(sketch, "E56.right", {"start": v(-162.48, -277.03) * mm, "end": v(-162.48, -398.17) * mm});
            skLineSegment(sketch, "E57.bottom", {"start": v(-66.64, -295.14) * mm, "end": v(-28.22, -295.14) * mm});
            skLineSegment(sketch, "E57.top", {"start": v(-66.64, -398.17) * mm, "end": v(-28.22, -398.17) * mm});
            skLineSegment(sketch, "E57.left", {"start": v(-66.64, -295.14) * mm, "end": v(-66.64, -398.17) * mm});
            skLineSegment(sketch, "E57.right", {"start": v(-28.22, -295.14) * mm, "end": v(-28.22, -398.17) * mm});
            skLineSegment(sketch, "E58.bottom", {"start": v(80.04, -293.06) * mm, "end": v(117.2, -293.06) * mm});
            skLineSegment(sketch, "E58.top", {"start": v(80.04, -398.17) * mm, "end": v(117.2, -398.17) * mm});
            skLineSegment(sketch, "E58.left", {"start": v(80.04, -293.06) * mm, "end": v(80.04, -398.17) * mm});
            skLineSegment(sketch, "E58.right", {"start": v(117.2, -293.06) * mm, "end": v(117.2, -398.17) * mm});
            skLineSegment(sketch, "E59.bottom", {"start": v(0, -302.45) * mm, "end": v(36.5, -302.45) * mm});
            skLineSegment(sketch, "E59.top", {"start": v(0, -398.17) * mm, "end": v(36.5, -398.17) * mm});
            skLineSegment(sketch, "E59.left", {"start": v(0, -302.45) * mm, "end": v(0, -398.17) * mm});
            skLineSegment(sketch, "E59.right", {"start": v(36.5, -302.45) * mm, "end": v(36.5, -398.17) * mm});
            skLineSegment(sketch, "E60.bottom", {"start": v(184.47, -305.64) * mm, "end": v(219.04, -305.64) * mm});
            skLineSegment(sketch, "E60.top", {"start": v(184.47, -398.17) * mm, "end": v(219.04, -398.17) * mm});
            skLineSegment(sketch, "E60.left", {"start": v(184.47, -305.64) * mm, "end": v(184.47, -398.17) * mm});
            skLineSegment(sketch, "E60.right", {"start": v(219.04, -305.64) * mm, "end": v(219.04, -398.17) * mm});
            skSolve(sketch);
        }
        {
            var Q0;
            Q0 = qSketchRegion(id + "F44", true);
            extrude(context, id + "F45", {"entities" : qUnion([Q0]), "operationType" : NewBodyOperationType.ADD, "oppositeDirection" : true, "depth" : 25.4 * mm});
        }
        {
            var Q0;
            Q0=makeQuery(id+"F43.opExtrude","SWEPT_FACE",FACE,{"disambiguationData":[OSD([sQuery(id+"F42.wireOp",EDGE,"E54.top")])]});
            var sketch = newSketch(context, id + "F46", { "sketchPlane" : qUnion([Q0])});
            skLineSegment(sketch, "E61.bottom", {"start": v(-274.36, -288.22) * mm, "end": v(-203.18, -288.22) * mm});
            skLineSegment(sketch, "E61.top", {"start": v(-274.36, -398.17) * mm, "end": v(-203.18, -398.17) * mm});
            skLineSegment(sketch, "E61.left", {"start": v(-274.36, -288.22) * mm, "end": v(-274.36, -398.17) * mm});
            skLineSegment(sketch, "E61.right", {"start": v(-203.18, -288.22) * mm, "end": v(-203.18, -398.17) * mm});
            skLineSegment(sketch, "E62.bottom", {"start": v(-126.32, -289.8) * mm, "end": v(-74.14, -289.8) * mm});
            skLineSegment(sketch, "E62.top", {"start": v(-126.32, -398.17) * mm, "end": v(-74.14, -398.17) * mm});
            skLineSegment(sketch, "E62.left", {"start": v(-126.32, -289.8) * mm, "end": v(-126.32, -398.17) * mm});
            skLineSegment(sketch, "E62.right", {"start": v(-74.14, -289.8) * mm, "end": v(-74.14, -398.17) * mm});
            skLineSegment(sketch, "E63.bottom", {"start": v(0, -285.59) * mm, "end": v(45.46, -285.59) * mm});
            skLineSegment(sketch, "E63.top", {"start": v(0, -398.17) * mm, "end": v(45.46, -398.17) * mm});
            skLineSegment(sketch, "E63.left", {"start": v(0, -285.59) * mm, "end": v(0, -398.17) * mm});
            skLineSegment(sketch, "E63.right", {"start": v(45.46, -285.59) * mm, "end": v(45.46, -398.17) * mm});
            skLineSegment(sketch, "E64.bottom", {"start": v(111.76, -301.86) * mm, "end": v(161.23, -301.86) * mm});
            skLineSegment(sketch, "E64.top", {"start": v(111.76, -398.17) * mm, "end": v(161.23, -398.17) * mm});
            skLineSegment(sketch, "E64.left", {"start": v(111.76, -301.86) * mm, "end": v(111.76, -398.17) * mm});
            skLineSegment(sketch, "E64.right", {"start": v(161.23, -301.86) * mm, "end": v(161.23, -398.17) * mm});
            skLineSegment(sketch, "E65.bottom", {"start": v(207.04, -300.42) * mm, "end": v(324.85, -300.42) * mm});
            skLineSegment(sketch, "E65.top", {"start": v(207.04, -398.17) * mm, "end": v(324.85, -398.17) * mm});
            skLineSegment(sketch, "E65.left", {"start": v(207.04, -300.42) * mm, "end": v(207.04, -398.17) * mm});
            skLineSegment(sketch, "E65.right", {"start": v(324.85, -300.42) * mm, "end": v(324.85, -398.17) * mm});
            skSolve(sketch);
        }
        {
            var Q0;
            Q0 = qSketchRegion(id + "F46", true);
            extrude(context, id + "F47", {"entities" : qUnion([Q0]), "operationType" : NewBodyOperationType.ADD, "oppositeDirection" : true, "depth" : 25.4 * mm});
        }
        {
            var Q0;
            Q0=makeQuery(id+"F47.boolean.opBoolean","MERGE",FACE,{"derivedFrom":[makeQuery(id+"F43.opExtrude","SWEPT_FACE",FACE,{"disambiguationData":[OSD([sQuery(id+"F42.wireOp",EDGE,"E54.right")])]}),makeQuery(id+"F47.opExtrude","SWEPT_FACE",FACE,{"disambiguationData":[OSD([sQuery(id+"F46.wireOp",EDGE,"E65.right")])]})]});
            var sketch = newSketch(context, id + "F48", { "sketchPlane" : qUnion([Q0])});
            skLineSegment(sketch, "E66.bottom", {"start": v(-265.2, -300.42) * mm, "end": v(-217.6, -300.42) * mm});
            skLineSegment(sketch, "E66.top", {"start": v(-265.2, -398.17) * mm, "end": v(-217.6, -398.17) * mm});
            skLineSegment(sketch, "E66.left", {"start": v(-265.2, -300.42) * mm, "end": v(-265.2, -398.17) * mm});
            skLineSegment(sketch, "E66.right", {"start": v(-217.6, -300.42) * mm, "end": v(-217.6, -398.17) * mm});
            skLineSegment(sketch, "E67.bottom", {"start": v(-167.25, -300.42) * mm, "end": v(-120.27, -300.42) * mm});
            skLineSegment(sketch, "E67.top", {"start": v(-167.25, -398.17) * mm, "end": v(-120.27, -398.17) * mm});
            skLineSegment(sketch, "E67.left", {"start": v(-167.25, -300.42) * mm, "end": v(-167.25, -398.17) * mm});
            skLineSegment(sketch, "E67.right", {"start": v(-120.27, -300.42) * mm, "end": v(-120.27, -398.17) * mm});
            skLineSegment(sketch, "E68.bottom", {"start": v(-72.65, -298.28) * mm, "end": v(-33.04, -298.28) * mm});
            skLineSegment(sketch, "E68.top", {"start": v(-72.65, -398.17) * mm, "end": v(-33.04, -398.17) * mm});
            skLineSegment(sketch, "E68.left", {"start": v(-72.65, -298.28) * mm, "end": v(-72.65, -398.17) * mm});
            skLineSegment(sketch, "E68.right", {"start": v(-33.04, -298.28) * mm, "end": v(-33.04, -398.17) * mm});
            skLineSegment(sketch, "E69.bottom", {"start": v(24.66, -300.42) * mm, "end": v(0, -300.42) * mm});
            skLineSegment(sketch, "E69.top", {"start": v(24.66, -398.17) * mm, "end": v(0, -398.17) * mm});
            skLineSegment(sketch, "E69.left", {"start": v(24.66, -300.42) * mm, "end": v(24.66, -398.17) * mm});
            skLineSegment(sketch, "E69.right", {"start": v(0, -300.42) * mm, "end": v(0, -398.17) * mm});
            skSolve(sketch);
        }
        {
            var Q0;
            Q0 = qSketchRegion(id + "F48", true);
            extrude(context, id + "F49", {"entities" : qUnion([Q0]), "operationType" : NewBodyOperationType.ADD, "oppositeDirection" : true, "depth" : 25.4 * mm});
        }
        {
            var Q0;
            Q0=makeQuery(id+"F43.opExtrude","SWEPT_FACE",FACE,{"disambiguationData":[OSD([sQuery(id+"F42.wireOp",EDGE,"E54.left")])]});
            var sketch = newSketch(context, id + "F50", { "sketchPlane" : qUnion([Q0])});
            skLineSegment(sketch, "E70.bottom", {"start": v(-24.66, -347.37) * mm, "end": v(239.8, -347.37) * mm});
            skLineSegment(sketch, "E70.top", {"start": v(-24.66, -398.17) * mm, "end": v(239.8, -398.17) * mm});
            skLineSegment(sketch, "E70.left", {"start": v(-24.66, -347.37) * mm, "end": v(-24.66, -398.17) * mm});
            skLineSegment(sketch, "E70.right", {"start": v(239.8, -347.37) * mm, "end": v(239.8, -398.17) * mm});
            skSolve(sketch);
        }
        {
            var Q0;
            Q0 = qSketchRegion(id + "F50", true);
            extrude(context, id + "F51", {"entities" : qUnion([Q0]), "operationType" : NewBodyOperationType.ADD, "depth" : 254 * mm});
        }
        {
            var Q0;
            Q0=makeQuery(id+"F51.boolean.opBoolean","MERGE",FACE,{"derivedFrom":[makeQuery(id+"F43.opExtrude","CAP_FACE",FACE,{"disambiguationData":[OSD([sQuery(id+"F42.wireOp",EDGE,"E54.bottom"),sQuery(id+"F42.wireOp",EDGE,"E54.top"),sQuery(id+"F42.wireOp",EDGE,"E54.left"),sQuery(id+"F42.wireOp",EDGE,"E54.right")])],"isStart":true}),makeQuery(id+"F51.opExtrude","SWEPT_FACE",FACE,{"disambiguationData":[OSD([sQuery(id+"F50.wireOp",EDGE,"E70.bottom")])]})]});
            var sketch = newSketch(context, id + "F52", { "sketchPlane" : qUnion([Q0])});
            skCircle(sketch, "E71", {"center": v(-281.62, 0) * mm, "radius": 49 * mm});
            skSolve(sketch);
        }
        {
            var Q0;
            Q0 = qSketchRegion(id + "F52", true);
            extrude(context, id + "F53", {"entities" : qUnion([Q0]), "operationType" : NewBodyOperationType.ADD, "depth" : 635 * mm});
        }
        {
            var Q0;
            Q0=makeQuery(id+"F51.boolean.opBoolean","MERGE",FACE,{"derivedFrom":[makeQuery(id+"F43.opExtrude","CAP_FACE",FACE,{"disambiguationData":[OSD([sQuery(id+"F42.wireOp",EDGE,"E54.bottom"),sQuery(id+"F42.wireOp",EDGE,"E54.top"),sQuery(id+"F42.wireOp",EDGE,"E54.left"),sQuery(id+"F42.wireOp",EDGE,"E54.right")])],"isStart":true}),makeQuery(id+"F51.opExtrude","SWEPT_FACE",FACE,{"disambiguationData":[OSD([sQuery(id+"F50.wireOp",EDGE,"E70.bottom")])]})]});
            var sketch = newSketch(context, id + "F54", { "sketchPlane" : qUnion([Q0])});
            skCircle(sketch, "E72", {"center": v(-305.66, -218.6) * mm, "radius": 36.96 * mm});
            skPoint(sketch, "E72.centerSnap0", {"position": v(-143.4, -218.6) * mm});
            skSolve(sketch);
        }
        {
            var Q0;
            Q0 = qSketchRegion(id + "F54", true);
            extrude(context, id + "F55", {"entities" : qUnion([Q0]), "operationType" : NewBodyOperationType.ADD, "depth" : 635 * mm});
        }
        {
            var Q0;
            Q0=makeQuery(id+"F53.opExtrude","CAP_FACE",FACE,{"disambiguationData":[OSD([sQuery(id+"F52.wireOp",EDGE,"E71")])],"isStart":false});
            fillet(context, id + "F56", {"entities" : qUnion([Q0]), "radius" : 48.26 * mm, "tangentPropagation" : true, "allowEdgeOverflow" : false});
        }
        {
            var Q0;
            Q0=makeQuery(id+"F55.opExtrude","CAP_EDGE",EDGE,{"disambiguationData":[OSD([sQuery(id+"F54.wireOp",EDGE,"E72")])],"isStart":false});
            fillet(context, id + "F57", {"entities" : qUnion([Q0]), "radius" : 35.56 * mm, "tangentPropagation" : true, "allowEdgeOverflow" : false});
        }
        {
            var Q0;
            Q0=makeQuery(id+"F51.opExtrude","CAP_FACE",FACE,{"disambiguationData":[OSD([sQuery(id+"F50.wireOp",EDGE,"E70.bottom"),sQuery(id+"F50.wireOp",EDGE,"E70.top"),sQuery(id+"F50.wireOp",EDGE,"E70.left"),sQuery(id+"F50.wireOp",EDGE,"E70.right")])],"isStart":false});
            var sketch = newSketch(context, id + "F58", { "sketchPlane" : qUnion([Q0])});
            skLineSegment(sketch, "E73.bottom", {"start": v(-24.66, -347.37) * mm, "end": v(239.8, -347.37) * mm});
            skLineSegment(sketch, "E73.top", {"start": v(-24.66, -398.17) * mm, "end": v(239.8, -398.17) * mm});
            skLineSegment(sketch, "E73.left", {"start": v(-24.66, -347.37) * mm, "end": v(-24.66, -398.17) * mm});
            skLineSegment(sketch, "E73.right", {"start": v(239.8, -347.37) * mm, "end": v(239.8, -398.17) * mm});
            skSolve(sketch);
        }
        {
            var Q0;
            Q0 = qSketchRegion(id + "F58", true);
            extrude(context, id + "F59", {"entities" : qUnion([Q0]), "operationType" : NewBodyOperationType.ADD, "depth" : 508 * mm});
        }
        {
            var Q0;
            Q0=makeQuery(id+"F59.boolean.opBoolean","MERGE",FACE,{"derivedFrom":[makeQuery(id+"F51.boolean.opBoolean","MERGE",FACE,{"derivedFrom":[makeQuery(id+"F43.opExtrude","CAP_FACE",FACE,{"disambiguationData":[OSD([sQuery(id+"F42.wireOp",EDGE,"E54.bottom"),sQuery(id+"F42.wireOp",EDGE,"E54.top"),sQuery(id+"F42.wireOp",EDGE,"E54.left"),sQuery(id+"F42.wireOp",EDGE,"E54.right")])],"isStart":true}),makeQuery(id+"F51.opExtrude","SWEPT_FACE",FACE,{"disambiguationData":[OSD([sQuery(id+"F50.wireOp",EDGE,"E70.bottom")])]})]}),makeQuery(id+"F59.opExtrude","SWEPT_FACE",FACE,{"disambiguationData":[OSD([sQuery(id+"F58.wireOp",EDGE,"E73.bottom")])]})]});
            var sketch = newSketch(context, id + "F60", { "sketchPlane" : qUnion([Q0])});
            skCircle(sketch, "E74", {"center": v(-555.85, -82.27) * mm, "radius": 117.03 * mm});
            skSolve(sketch);
        }
        {
            var Q0;
            Q0 = qSketchRegion(id + "F60", true);
            extrude(context, id + "F61", {"entities" : qUnion([Q0]), "operationType" : NewBodyOperationType.ADD, "depth" : 1270 * mm});
        }
        {
            var Q0;
            Q0=makeQuery(id+"F61.opExtrude","CAP_FACE",FACE,{"disambiguationData":[OSD([sQuery(id+"F60.wireOp",EDGE,"E74")])],"isStart":false});
            var sketch = newSketch(context, id + "F62", { "sketchPlane" : qUnion([Q0])});
            skCircle(sketch, "E75", {"center": v(-555.85, -82.27) * mm, "radius": 77.2 * mm});
            skSolve(sketch);
        }
        {
            var Q0;
            Q0 = qSketchRegion(id + "F62", true);
            extrude(context, id + "F63", {"entities" : qUnion([Q0]), "operationType" : NewBodyOperationType.REMOVE, "oppositeDirection" : true, "depth" : 381 * mm});
        }
        {
            var Q0;
            Q0=makeQuery(id+"F61.opExtrude","CAP_FACE",FACE,{"disambiguationData":[OSD([sQuery(id+"F60.wireOp",EDGE,"E74")])],"isStart":false});
            var sketch = newSketch(context, id + "F64", { "sketchPlane" : qUnion([Q0])});
            skLineSegment(sketch, "E76.bottom", {"start": v(-628.04, -54.93) * mm, "end": v(-671.82, -54.93) * mm});
            skLineSegment(sketch, "E76.top", {"start": v(-628.04, -97.97) * mm, "end": v(-671.82, -97.97) * mm});
            skLineSegment(sketch, "E76.left", {"start": v(-628.04, -54.93) * mm, "end": v(-628.04, -97.97) * mm});
            skLineSegment(sketch, "E76.right", {"start": v(-671.82, -54.93) * mm, "end": v(-671.82, -97.97) * mm});
            skLineSegment(sketch, "E77.bottom", {"start": v(-607.7, -139.47) * mm, "end": v(-571.27, -139.47) * mm});
            skLineSegment(sketch, "E77.top", {"start": v(-607.7, -198.28) * mm, "end": v(-571.27, -198.28) * mm});
            skLineSegment(sketch, "E77.left", {"start": v(-607.7, -139.47) * mm, "end": v(-607.7, -198.28) * mm});
            skLineSegment(sketch, "E77.right", {"start": v(-571.27, -139.47) * mm, "end": v(-571.27, -198.28) * mm});
            skLineSegment(sketch, "E78.bottom", {"start": v(-516.54, -148.7) * mm, "end": v(-483.24, -148.7) * mm});
            skLineSegment(sketch, "E78.top", {"start": v(-516.54, -174.04) * mm, "end": v(-483.24, -174.04) * mm});
            skLineSegment(sketch, "E78.left", {"start": v(-516.54, -148.7) * mm, "end": v(-516.54, -174.04) * mm});
            skLineSegment(sketch, "E78.right", {"start": v(-483.24, -148.7) * mm, "end": v(-483.24, -174.04) * mm});
            skLineSegment(sketch, "E79.bottom", {"start": v(-572.98, -7) * mm, "end": v(-604.77, -7) * mm});
            skLineSegment(sketch, "E79.top", {"start": v(-572.98, 24.04) * mm, "end": v(-604.77, 24.04) * mm});
            skLineSegment(sketch, "E79.left", {"start": v(-572.98, -7) * mm, "end": v(-572.98, 24.04) * mm});
            skLineSegment(sketch, "E79.right", {"start": v(-604.77, -7) * mm, "end": v(-604.77, 24.04) * mm});
            skLineSegment(sketch, "E80.bottom", {"start": v(-472.63, 0) * mm, "end": v(-499.87, 0) * mm});
            skLineSegment(sketch, "E80.top", {"start": v(-472.63, -29.12) * mm, "end": v(-499.87, -29.12) * mm});
            skLineSegment(sketch, "E80.left", {"start": v(-472.63, 0) * mm, "end": v(-472.63, -29.12) * mm});
            skLineSegment(sketch, "E80.right", {"start": v(-499.87, 0) * mm, "end": v(-499.87, -29.12) * mm});
            skLineSegment(sketch, "E81.bottom", {"start": v(-439.93, -66.22) * mm, "end": v(-481.45, -66.22) * mm});
            skLineSegment(sketch, "E81.top", {"start": v(-439.93, -102.84) * mm, "end": v(-481.45, -102.84) * mm});
            skLineSegment(sketch, "E81.left", {"start": v(-439.93, -66.22) * mm, "end": v(-439.93, -102.84) * mm});
            skLineSegment(sketch, "E81.right", {"start": v(-481.45, -66.22) * mm, "end": v(-481.45, -102.84) * mm});
            skSolve(sketch);
        }
        {
            var Q0;
            Q0 = qSketchRegion(id + "F64", true);
            extrude(context, id + "F65", {"entities" : qUnion([Q0]), "operationType" : NewBodyOperationType.ADD, "depth" : 76.2 * mm});
        }
        {
            var Q0;
            Q0=makeQuery(id+"F59.boolean.opBoolean","MERGE",FACE,{"derivedFrom":[makeQuery(id+"F51.boolean.opBoolean","MERGE",FACE,{"derivedFrom":[makeQuery(id+"F43.opExtrude","CAP_FACE",FACE,{"disambiguationData":[OSD([sQuery(id+"F42.wireOp",EDGE,"E54.bottom"),sQuery(id+"F42.wireOp",EDGE,"E54.top"),sQuery(id+"F42.wireOp",EDGE,"E54.left"),sQuery(id+"F42.wireOp",EDGE,"E54.right")])],"isStart":true}),makeQuery(id+"F51.opExtrude","SWEPT_FACE",FACE,{"disambiguationData":[OSD([sQuery(id+"F50.wireOp",EDGE,"E70.bottom")])]})]}),makeQuery(id+"F59.opExtrude","SWEPT_FACE",FACE,{"disambiguationData":[OSD([sQuery(id+"F58.wireOp",EDGE,"E73.bottom")])]})]});
            var sketch = newSketch(context, id + "F66", { "sketchPlane" : qUnion([Q0])});
            skCircle(sketch, "E82", {"center": v(-807.84, -17.2) * mm, "radius": 7.62 * mm});
            skCircle(sketch, "E83", {"center": v(-804.1, -49.5) * mm, "radius": 7.62 * mm});
            skSolve(sketch);
        }
        {
            var Q0;
            Q0 = qSketchRegion(id + "F66", true);
            extrude(context, id + "F67", {"entities" : qUnion([Q0]), "operationType" : NewBodyOperationType.ADD, "depth" : 76.2 * mm});
        }
        {
            var Q0;
            Q0=makeQuery(id+"F67.opExtrude","CAP_FACE",FACE,{"disambiguationData":[OSD([sQuery(id+"F66.wireOp",EDGE,"E82")])],"isStart":false});
            var sketch = newSketch(context, id + "F68", { "sketchPlane" : qUnion([Q0])});
            skLineSegment(sketch, "E84.bottom", {"start": v(-803.87, -10.7) * mm, "end": v(-817.48, -10.7) * mm});
            skLineSegment(sketch, "E84.top", {"start": v(-803.87, -60.25) * mm, "end": v(-817.48, -60.25) * mm});
            skLineSegment(sketch, "E84.left", {"start": v(-803.87, -10.7) * mm, "end": v(-803.87, -60.25) * mm});
            skLineSegment(sketch, "E84.right", {"start": v(-817.48, -10.7) * mm, "end": v(-817.48, -60.25) * mm});
            skSolve(sketch);
        }
        {
            var Q0;
            Q0 = qSketchRegion(id + "F68", true);
            extrude(context, id + "F69", {"entities" : qUnion([Q0]), "operationType" : NewBodyOperationType.ADD, "depth" : 127 * mm});
        }
        {
            var Q0;
            Q0=makeQuery(id+"F69.opExtrude","SWEPT_FACE",FACE,{"disambiguationData":[OSD([sQuery(id+"F68.wireOp",EDGE,"E84.right")])]});
            var sketch = newSketch(context, id + "F70", { "sketchPlane" : qUnion([Q0])});
            skCircle(sketch, "E85", {"center": v(35.48, -121.55) * mm, "radius": 44.75 * mm});
            skPoint(sketch, "E85.centerSnap0", {"position": v(35.48, -144.17) * mm});
            skSolve(sketch);
        }
        {
            var Q0;
            Q0 = qSketchRegion(id + "F70", true);
            extrude(context, id + "F71", {"entities" : qUnion([Q0]), "operationType" : NewBodyOperationType.ADD, "oppositeDirection" : true, "depth" : 25.4 * mm});
        }
        {
            var Q0;
            Q0=makeQuery(id+"F69.opExtrude","SWEPT_FACE",FACE,{"disambiguationData":[OSD([sQuery(id+"F68.wireOp",EDGE,"E84.bottom")])]});
            var sketch = newSketch(context, id + "F72", { "sketchPlane" : qUnion([Q0])});
            skCircle(sketch, "E86", {"center": v(803.87, -189.82) * mm, "radius": 21.12 * mm});
            skSolve(sketch);
        }
        {
            var Q0;
            Q0 = qSketchRegion(id + "F72", true);
            extrude(context, id + "F73", {"entities" : qUnion([Q0]), "operationType" : NewBodyOperationType.ADD, "depth" : 76.2 * mm});
        }
        {
            var Q0;
            Q0=makeQuery(id+"F69.opExtrude","SWEPT_FACE",FACE,{"disambiguationData":[OSD([sQuery(id+"F68.wireOp",EDGE,"E84.top")])]});
            var sketch = newSketch(context, id + "F74", { "sketchPlane" : qUnion([Q0])});
            skCircle(sketch, "E87", {"center": v(-803.87, -215) * mm, "radius": 19.25 * mm});
            skSolve(sketch);
        }
        {
            var Q0;
            Q0 = qSketchRegion(id + "F74", true);
            extrude(context, id + "F75", {"entities" : qUnion([Q0]), "operationType" : NewBodyOperationType.ADD, "depth" : 76.2 * mm});
        }
        {
            var Q0;
            Q0=makeQuery(id+"F75.opExtrude","CAP_EDGE",EDGE,{"disambiguationData":[OSD([sQuery(id+"F74.wireOp",EDGE,"E87")])],"isStart":false});
            fillet(context, id + "F76", {"entities" : qUnion([Q0]), "radius" : 17.78 * mm, "tangentPropagation" : true, "allowEdgeOverflow" : false});
        }
        {
            var Q0;
            Q0=makeQuery(id+"F73.opExtrude","CAP_FACE",FACE,{"disambiguationData":[OSD([sQuery(id+"F72.wireOp",EDGE,"E86")])],"isStart":false});
            fillet(context, id + "F77", {"entities" : qUnion([Q0]), "radius" : 20.32 * mm, "tangentPropagation" : true, "allowEdgeOverflow" : false});
        }
    });
